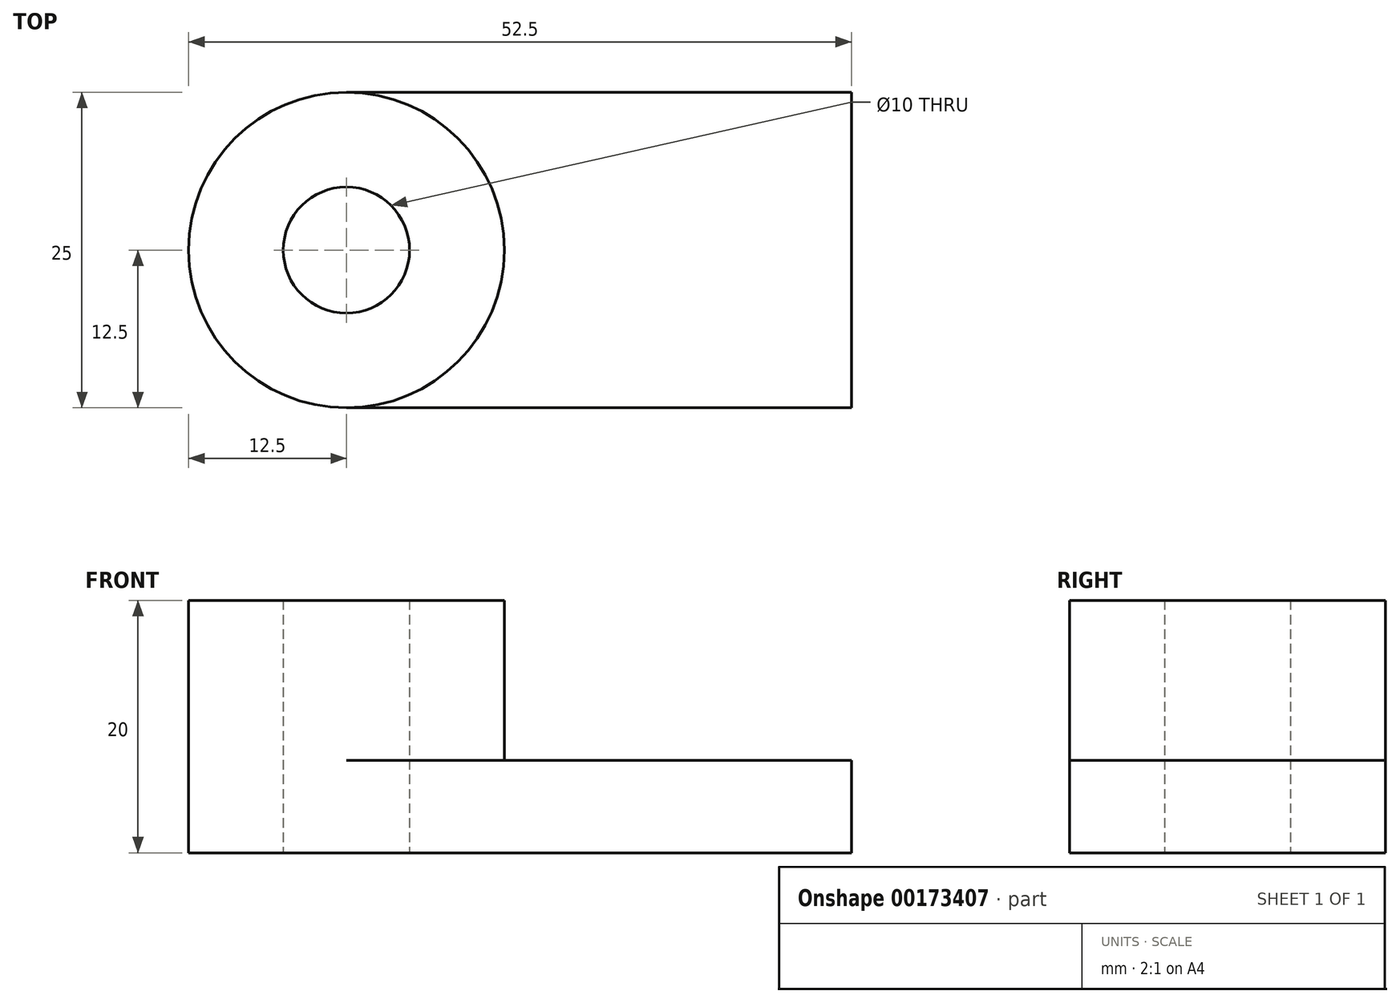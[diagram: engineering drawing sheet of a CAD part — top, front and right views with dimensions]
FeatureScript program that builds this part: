
annotation { "Feature Type Name" : "Feature", "Feature Type Description" : "" }
export const myFeature = defineFeature(function(context is Context, id is Id, definition is map)
    precondition{}
    {
        {
            var Q0;
            Q0=qCreatedBy(makeId("Top.planeOp"),FACE);
            var sketch = newSketch(context, id + "F0", { "sketchPlane" : qUnion([Q0])});
            skLineSegment(sketch, "E0.bottom", {"start": v(20, -12.5) * mm, "end": v(-20, -12.5) * mm});
            skLineSegment(sketch, "E0.top", {"start": v(20, 12.5) * mm, "end": v(-20, 12.5) * mm});
            skLineSegment(sketch, "E0.left", {"start": v(20, -12.5) * mm, "end": v(20, 12.5) * mm});
            skLineSegment(sketch, "E0.right", {"start": v(-20, -12.5) * mm, "end": v(-20, 12.5) * mm});
            skPoint(sketch, "E0.middle", {"position": v(0, 0) * mm});
            skCircle(sketch, "E1", {"center": v(-20, 0) * mm, "radius": 12.5 * mm});
            skCircle(sketch, "E2", {"center": v(-20, 0) * mm, "radius": 5 * mm});
            skSolve(sketch);
        }
        {
            var Q0;
            Q0 = qSketchRegion(id + "F0", true);
            var sketch = newSketch(context, id + "F1", { "sketchPlane" : qUnion([Q0])});
            skSolve(sketch);
        }
        {
            var Q0;
            Q0 = qSketchRegion(id + "F1", true);
            var Q1;
            {var subQ0=sQuery(id+"F0.wireOp",EDGE,"E0.bottom");Q1=makeQuery(id+"F0.imprint","IMPRINT",FACE,{"disambiguationData":[TD([[makeQuery(id+"F0.imprint","IMPRINT",EDGE,{"derivedFrom":subQ0}),-1.0]])]});}
            var Q2;
            {var subQ1=sQuery(id+"F0.wireOp",EDGE,"E0.right");var subQ3=sQuery(id+"F0.wireOp",EDGE,"E2");var subQ4=makeQuery(id+"F0.imprint","INTERSECT",VERTEX,{"disambiguationData":[OD(0.0)],"derivedFrom":[subQ1,subQ3]});Q2=makeQuery(id+"F0.imprint","IMPRINT",FACE,{"disambiguationData":[TD([[makeQuery(id+"F0.imprint","IMPRINT",EDGE,{"disambiguationData":[TD([[subQ4,-1.0]])],"derivedFrom":subQ3}),-1.0]])]});}
            var Q3;
            {var subQ1=sQuery(id+"F0.wireOp",EDGE,"E0.right");var subQ3=sQuery(id+"F0.wireOp",EDGE,"E2");var subQ4=makeQuery(id+"F0.imprint","INTERSECT",VERTEX,{"disambiguationData":[OD(0.0)],"derivedFrom":[subQ1,subQ3]});Q3=makeQuery(id+"F0.imprint","IMPRINT",FACE,{"disambiguationData":[TD([[makeQuery(id+"F0.imprint","IMPRINT",EDGE,{"disambiguationData":[TD([[subQ4,1.0]])],"derivedFrom":subQ3}),-1.0]])]});}
            extrude(context, id + "F2", {"entities" : qUnion([Q0, Q1, Q2, Q3]), "depth" : 7.3 * mm});
        }
        {
            var Q0;
            {var subQ1=sQuery(id+"F0.wireOp",EDGE,"E0.right");var subQ3=sQuery(id+"F0.wireOp",EDGE,"E2");var subQ4=makeQuery(id+"F0.imprint","INTERSECT",VERTEX,{"disambiguationData":[OD(0.0)],"derivedFrom":[subQ1,subQ3]});Q0=makeQuery(id+"F0.imprint","IMPRINT",FACE,{"disambiguationData":[TD([[makeQuery(id+"F0.imprint","IMPRINT",EDGE,{"disambiguationData":[TD([[subQ4,1.0]])],"derivedFrom":subQ3}),-1.0]])]});}
            var Q1;
            {var subQ1=sQuery(id+"F0.wireOp",EDGE,"E0.right");var subQ3=sQuery(id+"F0.wireOp",EDGE,"E2");var subQ4=makeQuery(id+"F0.imprint","INTERSECT",VERTEX,{"disambiguationData":[OD(0.0)],"derivedFrom":[subQ1,subQ3]});Q1=makeQuery(id+"F0.imprint","IMPRINT",FACE,{"disambiguationData":[TD([[makeQuery(id+"F0.imprint","IMPRINT",EDGE,{"disambiguationData":[TD([[subQ4,-1.0]])],"derivedFrom":subQ3}),-1.0]])]});}
            extrude(context, id + "F3", {"entities" : qUnion([Q0, Q1]), "operationType" : NewBodyOperationType.ADD, "depth" : 20 * mm});
        }
    });
